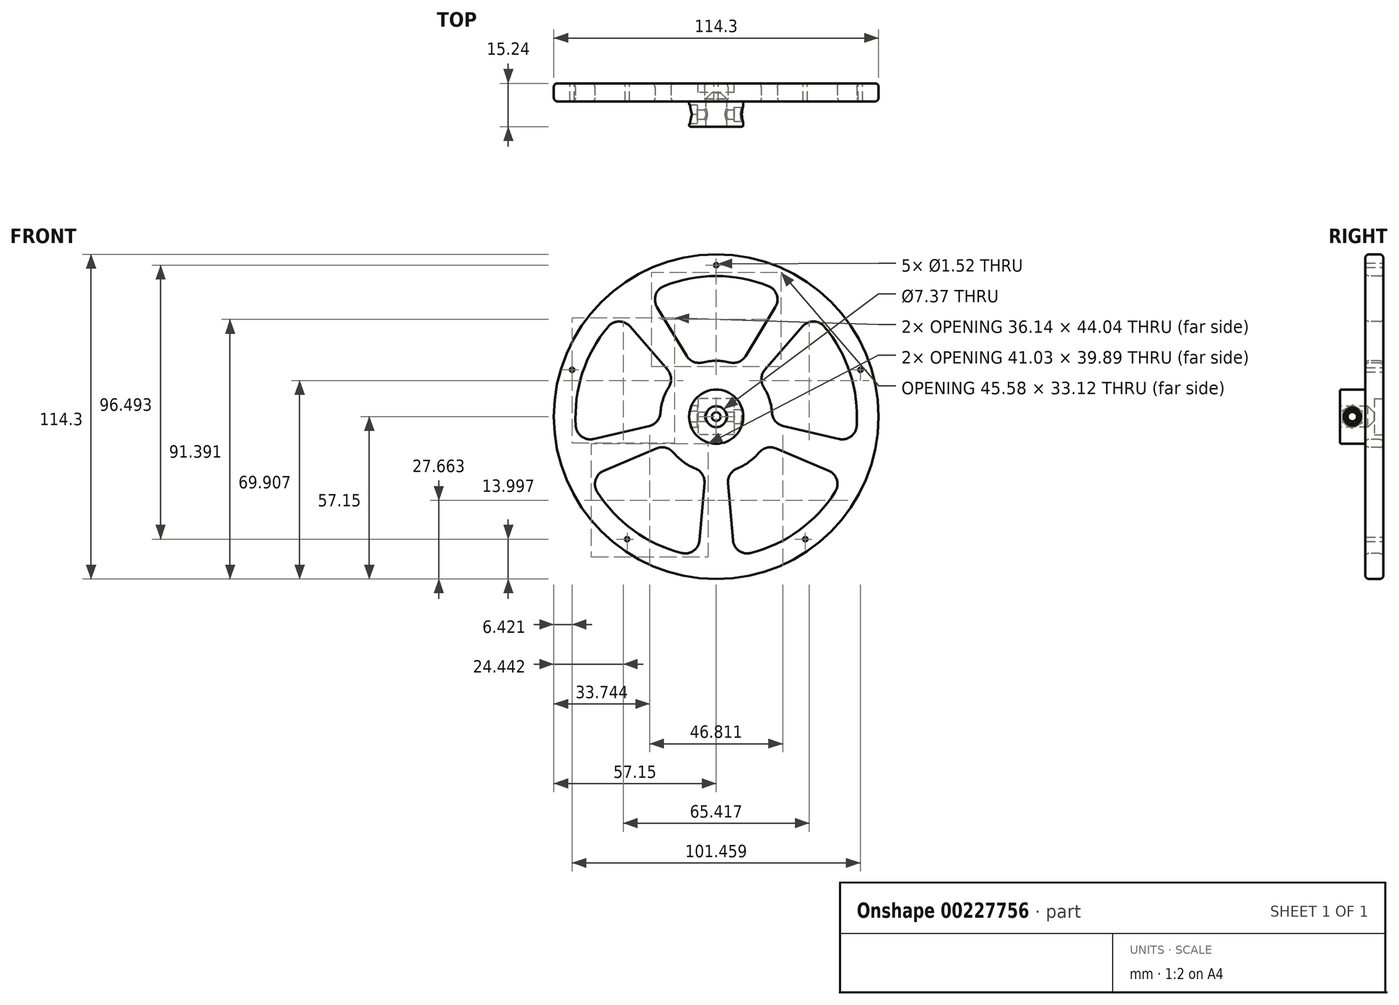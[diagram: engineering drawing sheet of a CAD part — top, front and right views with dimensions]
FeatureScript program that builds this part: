
annotation { "Feature Type Name" : "Feature", "Feature Type Description" : "" }
export const myFeature = defineFeature(function(context is Context, id is Id, definition is map)
    precondition{}
    {
        {
            var Q0;
            Q0=qCreatedBy(makeId("Front.planeOp"),FACE);
            var sketch = newSketch(context, id + "F0", { "sketchPlane" : qUnion([Q0])});
            skCircle(sketch, "E0", {"center": v(0, 0) * mm, "radius": 57.15 * mm});
            skSolve(sketch);
        }
        {
            var Q0;
            Q0 = qSketchRegion(id + "F0", true);
            extrude(context, id + "F1", {"entities" : qUnion([Q0]), "depth" : 6.35 * mm});
        }
        {
            var Q0;
            Q0=makeQuery(id+"F1.opExtrude","CAP_FACE",FACE,{"disambiguationData":[OSD([sQuery(id+"F0.wireOp",EDGE,"E0")])],"isStart":false});
            var sketch = newSketch(context, id + "F2", { "sketchPlane" : qUnion([Q0])});
            skCircle(sketch, "E1", {"center": v(0, 0) * mm, "radius": 9.53 * mm});
            skSolve(sketch);
        }
        {
            var Q0;
            Q0 = qSketchRegion(id + "F2", true);
            extrude(context, id + "F3", {"entities" : qUnion([Q0]), "operationType" : NewBodyOperationType.ADD, "depth" : 8.9 * mm});
        }
        {
            var Q0;
            Q0=makeQuery(id+"F3.opExtrude","CAP_FACE",FACE,{"disambiguationData":[OSD([sQuery(id+"F2.wireOp",EDGE,"E1")])],"isStart":false});
            var sketch = newSketch(context, id + "F4", { "sketchPlane" : qUnion([Q0])});
            skCircle(sketch, "E2", {"center": v(0, 0) * mm, "radius": 3.68 * mm});
            skSolve(sketch);
        }
        {
            var Q0;
            Q0 = qSketchRegion(id + "F4", true);
            extrude(context, id + "F5", {"entities" : qUnion([Q0]), "operationType" : NewBodyOperationType.REMOVE, "oppositeDirection" : true, "depth" : 8.9 * mm});
        }
        {
            var Q0;
            Q0=qCreatedBy(makeId("Right.planeOp"),FACE);
            var sketch = newSketch(context, id + "F6", { "sketchPlane" : qUnion([Q0])});
            skCircle(sketch, "E3", {"center": v(-10.92, 0) * mm, "radius": 1.65 * mm});
            skSolve(sketch);
        }
        {
            var Q0;
            Q0 = qSketchRegion(id + "F6", true);
            extrude(context, id + "F7", {"entities" : qUnion([Q0]), "operationType" : NewBodyOperationType.REMOVE, "oppositeDirection" : true, "depth" : 25.4 * mm, "symmetric" : true});
        }
        {
            var Q0;
            Q0=makeQuery(id+"F1.opExtrude","CAP_FACE",FACE,{"disambiguationData":[OSD([sQuery(id+"F0.wireOp",EDGE,"E0")])],"isStart":true});
            var sketch = newSketch(context, id + "F8", { "sketchPlane" : qUnion([Q0])});
            skCircle(sketch, "E4", {"center": v(0, 53.34) * mm, "radius": 0.76 * mm});
            skCircle(sketch, "E5.1.0", {"center": v(-50.73, 16.48) * mm, "radius": 0.76 * mm});
            skCircle(sketch, "E5.2.0", {"center": v(-31.35, -43.15) * mm, "radius": 0.76 * mm});
            skCircle(sketch, "E5.3.0", {"center": v(31.35, -43.15) * mm, "radius": 0.76 * mm});
            skCircle(sketch, "E5.4.0", {"center": v(50.73, 16.48) * mm, "radius": 0.76 * mm});
            skPoint(sketch, "E5.center", {"position": v(0, 0) * mm});
            skSolve(sketch);
        }
        {
            var Q0;
            Q0 = qSketchRegion(id + "F8", true);
            extrude(context, id + "F9", {"entities" : qUnion([Q0]), "operationType" : NewBodyOperationType.REMOVE, "endBound" : BoundingType.THROUGH_ALL, "oppositeDirection" : true, "depth" : 25.4 * mm});
        }
        {
            var Q0;
            Q0=makeQuery(id+"F1.opExtrude","CAP_FACE",FACE,{"disambiguationData":[OSD([sQuery(id+"F0.wireOp",EDGE,"E0")])],"isStart":false});
            var sketch = newSketch(context, id + "F10", { "sketchPlane" : qUnion([Q0])});
            skArc(sketch, "E6", {"start": v(-14.43, 13.38) * mm, "mid": v(-18.72, 6.08) * mm, "end": v(-19.54, -2.34) * mm});
            skArc(sketch, "E7", {"start": v(-34.01, 36) * mm, "mid": v(-47.1, 15.3) * mm, "end": v(-48.68, -9.14) * mm});
            skLineSegment(sketch, "E8", {"start": v(-3.8, -19.31) * mm, "end": v(-6.35, -49.12) * mm});
            skLineSegment(sketch, "E9", {"start": v(3.8, -19.31) * mm, "end": v(6.35, -49.12) * mm});
            skLineSegment(sketch, "E10.1.0", {"start": v(17.2, -9.6) * mm, "end": v(44.75, -21.22) * mm});
            skLineSegment(sketch, "E10.1.1", {"start": v(19.54, -2.34) * mm, "end": v(48.68, -9.14) * mm});
            skLineSegment(sketch, "E10.2.0", {"start": v(14.43, 13.38) * mm, "end": v(34.01, 36) * mm});
            skLineSegment(sketch, "E10.2.1", {"start": v(8.27, 17.86) * mm, "end": v(23.74, 43.47) * mm});
            skLineSegment(sketch, "E10.3.0", {"start": v(-8.27, 17.86) * mm, "end": v(-23.74, 43.47) * mm});
            skLineSegment(sketch, "E10.3.1", {"start": v(-14.43, 13.38) * mm, "end": v(-34.01, 36) * mm});
            skLineSegment(sketch, "E10.4.0", {"start": v(-19.54, -2.34) * mm, "end": v(-48.68, -9.14) * mm});
            skLineSegment(sketch, "E10.4.1", {"start": v(-17.2, -9.6) * mm, "end": v(-44.75, -21.22) * mm});
            skArc(sketch, "E11.trimOffspring", {"start": v(8.27, 17.86) * mm, "mid": v(0, 19.69) * mm, "end": v(-8.27, 17.86) * mm});
            skArc(sketch, "E12.trimOffspring", {"start": v(23.74, 43.47) * mm, "mid": v(0, 49.53) * mm, "end": v(-23.74, 43.47) * mm});
            skArc(sketch, "E13.trimOffspring", {"start": v(48.68, -9.14) * mm, "mid": v(47.1, 15.3) * mm, "end": v(34.01, 36) * mm});
            skArc(sketch, "E14.trimOffspring", {"start": v(19.54, -2.34) * mm, "mid": v(18.72, 6.08) * mm, "end": v(14.43, 13.38) * mm});
            skArc(sketch, "E15.trimOffspring", {"start": v(3.81, -19.31) * mm, "mid": v(11.57, -15.93) * mm, "end": v(17.2, -9.6) * mm});
            skArc(sketch, "E16.trimOffspring", {"start": v(6.35, -49.12) * mm, "mid": v(29.11, -40.07) * mm, "end": v(44.75, -21.22) * mm});
            skArc(sketch, "E17.trimOffspring", {"start": v(-44.75, -21.22) * mm, "mid": v(-29.11, -40.07) * mm, "end": v(-6.35, -49.12) * mm});
            skArc(sketch, "E18.trimOffspring", {"start": v(-17.2, -9.6) * mm, "mid": v(-11.57, -15.93) * mm, "end": v(-3.81, -19.31) * mm});
            skSolve(sketch);
        }
        {
            var Q0;
            Q0 = qSketchRegion(id + "F10", true);
            extrude(context, id + "F11", {"entities" : qUnion([Q0]), "operationType" : NewBodyOperationType.REMOVE, "oppositeDirection" : true, "depth" : 25.4 * mm});
        }
        {
            var Q0;
            Q0=makeQuery(id+"F11.boolean.opBoolean","COPY",EDGE,{"derivedFrom":makeQuery(id+"F11.opExtrude","SWEPT_EDGE",EDGE,{"disambiguationData":[OSD([sQuery(id+"F10.wireOp",EDGE,"E10.3.0"),sQuery(id+"F10.wireOp",EDGE,"E11.trimOffspring")])]})});
            var Q1;
            Q1=makeQuery(id+"F11.boolean.opBoolean","COPY",EDGE,{"derivedFrom":makeQuery(id+"F11.opExtrude","SWEPT_EDGE",EDGE,{"disambiguationData":[OSD([sQuery(id+"F10.wireOp",EDGE,"E10.2.1"),sQuery(id+"F10.wireOp",EDGE,"E11.trimOffspring")])]})});
            var Q2;
            Q2=makeQuery(id+"F11.boolean.opBoolean","COPY",EDGE,{"derivedFrom":makeQuery(id+"F11.opExtrude","SWEPT_EDGE",EDGE,{"disambiguationData":[OSD([sQuery(id+"F10.wireOp",EDGE,"E10.3.0"),sQuery(id+"F10.wireOp",EDGE,"E12.trimOffspring")])]})});
            var Q3;
            Q3=makeQuery(id+"F11.boolean.opBoolean","COPY",EDGE,{"derivedFrom":makeQuery(id+"F11.opExtrude","SWEPT_EDGE",EDGE,{"disambiguationData":[OSD([sQuery(id+"F10.wireOp",EDGE,"E10.2.1"),sQuery(id+"F10.wireOp",EDGE,"E12.trimOffspring")])]})});
            var Q4;
            Q4=makeQuery(id+"F11.boolean.opBoolean","COPY",EDGE,{"derivedFrom":makeQuery(id+"F11.opExtrude","SWEPT_EDGE",EDGE,{"disambiguationData":[OSD([sQuery(id+"F10.wireOp",EDGE,"E10.2.0"),sQuery(id+"F10.wireOp",EDGE,"E13.trimOffspring")])]})});
            var Q5;
            Q5=makeQuery(id+"F11.boolean.opBoolean","COPY",EDGE,{"derivedFrom":makeQuery(id+"F11.opExtrude","SWEPT_EDGE",EDGE,{"disambiguationData":[OSD([sQuery(id+"F10.wireOp",EDGE,"E10.2.0"),sQuery(id+"F10.wireOp",EDGE,"E14.trimOffspring")])]})});
            var Q6;
            Q6=makeQuery(id+"F11.boolean.opBoolean","COPY",EDGE,{"derivedFrom":makeQuery(id+"F11.opExtrude","SWEPT_EDGE",EDGE,{"disambiguationData":[OSD([sQuery(id+"F10.wireOp",EDGE,"E10.1.1"),sQuery(id+"F10.wireOp",EDGE,"E14.trimOffspring")])]})});
            var Q7;
            Q7=makeQuery(id+"F11.boolean.opBoolean","COPY",EDGE,{"derivedFrom":makeQuery(id+"F11.opExtrude","SWEPT_EDGE",EDGE,{"disambiguationData":[OSD([sQuery(id+"F10.wireOp",EDGE,"E10.1.1"),sQuery(id+"F10.wireOp",EDGE,"E13.trimOffspring")])]})});
            var Q8;
            Q8=makeQuery(id+"F11.boolean.opBoolean","COPY",EDGE,{"derivedFrom":makeQuery(id+"F11.opExtrude","SWEPT_EDGE",EDGE,{"disambiguationData":[OSD([sQuery(id+"F10.wireOp",EDGE,"E10.1.0"),sQuery(id+"F10.wireOp",EDGE,"E16.trimOffspring")])]})});
            var Q9;
            Q9=makeQuery(id+"F11.boolean.opBoolean","COPY",EDGE,{"derivedFrom":makeQuery(id+"F11.opExtrude","SWEPT_EDGE",EDGE,{"disambiguationData":[OSD([sQuery(id+"F10.wireOp",EDGE,"E9"),sQuery(id+"F10.wireOp",EDGE,"E16.trimOffspring")])]})});
            var Q10;
            Q10=makeQuery(id+"F11.boolean.opBoolean","COPY",EDGE,{"derivedFrom":makeQuery(id+"F11.opExtrude","SWEPT_EDGE",EDGE,{"disambiguationData":[OSD([sQuery(id+"F10.wireOp",EDGE,"E9"),sQuery(id+"F10.wireOp",EDGE,"E15.trimOffspring")])]})});
            var Q11;
            Q11=makeQuery(id+"F11.boolean.opBoolean","COPY",EDGE,{"derivedFrom":makeQuery(id+"F11.opExtrude","SWEPT_EDGE",EDGE,{"disambiguationData":[OSD([sQuery(id+"F10.wireOp",EDGE,"E10.1.0"),sQuery(id+"F10.wireOp",EDGE,"E15.trimOffspring")])]})});
            var Q12;
            Q12=makeQuery(id+"F11.boolean.opBoolean","COPY",EDGE,{"derivedFrom":makeQuery(id+"F11.opExtrude","SWEPT_EDGE",EDGE,{"disambiguationData":[OSD([sQuery(id+"F10.wireOp",EDGE,"E10.4.1"),sQuery(id+"F10.wireOp",EDGE,"E18.trimOffspring")])]})});
            var Q13;
            Q13=makeQuery(id+"F11.boolean.opBoolean","COPY",EDGE,{"derivedFrom":makeQuery(id+"F11.opExtrude","SWEPT_EDGE",EDGE,{"disambiguationData":[OSD([sQuery(id+"F10.wireOp",EDGE,"E8"),sQuery(id+"F10.wireOp",EDGE,"E18.trimOffspring")])]})});
            var Q14;
            Q14=makeQuery(id+"F11.boolean.opBoolean","COPY",EDGE,{"derivedFrom":makeQuery(id+"F11.opExtrude","SWEPT_EDGE",EDGE,{"disambiguationData":[OSD([sQuery(id+"F10.wireOp",EDGE,"E8"),sQuery(id+"F10.wireOp",EDGE,"E17.trimOffspring")])]})});
            var Q15;
            Q15=makeQuery(id+"F11.boolean.opBoolean","COPY",EDGE,{"derivedFrom":makeQuery(id+"F11.opExtrude","SWEPT_EDGE",EDGE,{"disambiguationData":[OSD([sQuery(id+"F10.wireOp",EDGE,"E10.4.1"),sQuery(id+"F10.wireOp",EDGE,"E17.trimOffspring")])]})});
            var Q16;
            Q16=makeQuery(id+"F11.boolean.opBoolean","COPY",EDGE,{"derivedFrom":makeQuery(id+"F11.opExtrude","SWEPT_EDGE",EDGE,{"disambiguationData":[OSD([sQuery(id+"F10.wireOp",EDGE,"E7"),sQuery(id+"F10.wireOp",EDGE,"E10.4.0")])]})});
            var Q17;
            Q17=makeQuery(id+"F11.boolean.opBoolean","COPY",EDGE,{"derivedFrom":makeQuery(id+"F11.opExtrude","SWEPT_EDGE",EDGE,{"disambiguationData":[OSD([sQuery(id+"F10.wireOp",EDGE,"E6"),sQuery(id+"F10.wireOp",EDGE,"E10.4.0")])]})});
            var Q18;
            Q18=makeQuery(id+"F11.boolean.opBoolean","COPY",EDGE,{"derivedFrom":makeQuery(id+"F11.opExtrude","SWEPT_EDGE",EDGE,{"disambiguationData":[OSD([sQuery(id+"F10.wireOp",EDGE,"E6"),sQuery(id+"F10.wireOp",EDGE,"E10.3.1")])]})});
            var Q19;
            Q19=makeQuery(id+"F11.boolean.opBoolean","COPY",EDGE,{"derivedFrom":makeQuery(id+"F11.opExtrude","SWEPT_EDGE",EDGE,{"disambiguationData":[OSD([sQuery(id+"F10.wireOp",EDGE,"E7"),sQuery(id+"F10.wireOp",EDGE,"E10.3.1")])]})});
            fillet(context, id + "F12", {"entities" : qUnion([Q0, Q1, Q2, Q3, Q4, Q5, Q6, Q7, Q8, Q9, Q10, Q11, Q12, Q13, Q14, Q15, Q16, Q17, Q18, Q19]), "radius" : 5.08 * mm, "tangentPropagation" : true, "allowEdgeOverflow" : false});
        }
        {
            var Q0;
            Q0=makeQuery(id+"F1.opExtrude","CAP_EDGE",EDGE,{"disambiguationData":[OSD([sQuery(id+"F0.wireOp",EDGE,"E0")])],"isStart":false});
            var Q1;
            Q1=makeQuery(id+"F12.opFillet","BLEND_EDGE",EDGE,{"blendedFrom":[makeQuery(id+"F11.boolean.opBoolean","COPY",EDGE,{"derivedFrom":makeQuery(id+"F11.opExtrude","SWEPT_EDGE",EDGE,{"disambiguationData":[OSD([sQuery(id+"F10.wireOp",EDGE,"E10.2.0"),sQuery(id+"F10.wireOp",EDGE,"E13.trimOffspring")])]})}),makeQuery(id+"F1.opExtrude","CAP_FACE",FACE,{"disambiguationData":[OSD([sQuery(id+"F0.wireOp",EDGE,"E0")])],"isStart":false})],"blendedInto":[makeQuery(id+"F1.opExtrude","CAP_FACE",FACE,{"disambiguationData":[OSD([sQuery(id+"F0.wireOp",EDGE,"E0")])],"isStart":false})]});
            var Q2;
            Q2=makeQuery(id+"F12.opFillet","BLEND_EDGE",EDGE,{"blendedFrom":[makeQuery(id+"F11.boolean.opBoolean","COPY",EDGE,{"derivedFrom":makeQuery(id+"F11.opExtrude","SWEPT_EDGE",EDGE,{"disambiguationData":[OSD([sQuery(id+"F10.wireOp",EDGE,"E10.2.1"),sQuery(id+"F10.wireOp",EDGE,"E11.trimOffspring")])]})}),makeQuery(id+"F1.opExtrude","CAP_FACE",FACE,{"disambiguationData":[OSD([sQuery(id+"F0.wireOp",EDGE,"E0")])],"isStart":false})],"blendedInto":[makeQuery(id+"F1.opExtrude","CAP_FACE",FACE,{"disambiguationData":[OSD([sQuery(id+"F0.wireOp",EDGE,"E0")])],"isStart":false})]});
            var Q3;
            Q3=makeQuery(id+"F12.opFillet","BLEND_EDGE",EDGE,{"blendedFrom":[makeQuery(id+"F11.boolean.opBoolean","COPY",EDGE,{"derivedFrom":makeQuery(id+"F11.opExtrude","SWEPT_EDGE",EDGE,{"disambiguationData":[OSD([sQuery(id+"F10.wireOp",EDGE,"E10.1.0"),sQuery(id+"F10.wireOp",EDGE,"E15.trimOffspring")])]})}),makeQuery(id+"F1.opExtrude","CAP_FACE",FACE,{"disambiguationData":[OSD([sQuery(id+"F0.wireOp",EDGE,"E0")])],"isStart":false})],"blendedInto":[makeQuery(id+"F1.opExtrude","CAP_FACE",FACE,{"disambiguationData":[OSD([sQuery(id+"F0.wireOp",EDGE,"E0")])],"isStart":false})]});
            var Q4;
            Q4=makeQuery(id+"F12.opFillet","BLEND_EDGE",EDGE,{"blendedFrom":[makeQuery(id+"F11.boolean.opBoolean","COPY",EDGE,{"derivedFrom":makeQuery(id+"F11.opExtrude","SWEPT_EDGE",EDGE,{"disambiguationData":[OSD([sQuery(id+"F10.wireOp",EDGE,"E10.4.1"),sQuery(id+"F10.wireOp",EDGE,"E18.trimOffspring")])]})}),makeQuery(id+"F1.opExtrude","CAP_FACE",FACE,{"disambiguationData":[OSD([sQuery(id+"F0.wireOp",EDGE,"E0")])],"isStart":false})],"blendedInto":[makeQuery(id+"F1.opExtrude","CAP_FACE",FACE,{"disambiguationData":[OSD([sQuery(id+"F0.wireOp",EDGE,"E0")])],"isStart":false})]});
            var Q5;
            Q5=makeQuery(id+"F12.opFillet","BLEND_EDGE",EDGE,{"blendedFrom":[makeQuery(id+"F11.boolean.opBoolean","COPY",EDGE,{"derivedFrom":makeQuery(id+"F11.opExtrude","SWEPT_EDGE",EDGE,{"disambiguationData":[OSD([sQuery(id+"F10.wireOp",EDGE,"E6"),sQuery(id+"F10.wireOp",EDGE,"E10.3.1")])]})}),makeQuery(id+"F1.opExtrude","CAP_FACE",FACE,{"disambiguationData":[OSD([sQuery(id+"F0.wireOp",EDGE,"E0")])],"isStart":false})],"blendedInto":[makeQuery(id+"F1.opExtrude","CAP_FACE",FACE,{"disambiguationData":[OSD([sQuery(id+"F0.wireOp",EDGE,"E0")])],"isStart":false})]});
            var Q6;
            Q6=makeQuery(id+"F11.boolean.opBoolean","INTERSECT",EDGE,{"derivedFrom":[makeQuery(id+"F1.opExtrude","CAP_FACE",FACE,{"disambiguationData":[OSD([sQuery(id+"F0.wireOp",EDGE,"E0")])],"isStart":true}),makeQuery(id+"F11.opExtrude","SWEPT_FACE",FACE,{"disambiguationData":[OSD([sQuery(id+"F10.wireOp",EDGE,"E12.trimOffspring")])]})]});
            var Q7;
            Q7=makeQuery(id+"F11.boolean.opBoolean","INTERSECT",EDGE,{"derivedFrom":[makeQuery(id+"F1.opExtrude","CAP_FACE",FACE,{"disambiguationData":[OSD([sQuery(id+"F0.wireOp",EDGE,"E0")])],"isStart":true}),makeQuery(id+"F11.opExtrude","SWEPT_FACE",FACE,{"disambiguationData":[OSD([sQuery(id+"F10.wireOp",EDGE,"E10.2.0")])]})]});
            var Q8;
            Q8=makeQuery(id+"F11.boolean.opBoolean","INTERSECT",EDGE,{"derivedFrom":[makeQuery(id+"F1.opExtrude","CAP_FACE",FACE,{"disambiguationData":[OSD([sQuery(id+"F0.wireOp",EDGE,"E0")])],"isStart":true}),makeQuery(id+"F11.opExtrude","SWEPT_FACE",FACE,{"disambiguationData":[OSD([sQuery(id+"F10.wireOp",EDGE,"E10.1.0")])]})]});
            var Q9;
            Q9=makeQuery(id+"F12.opFillet","BLEND_EDGE",EDGE,{"blendedFrom":[makeQuery(id+"F11.boolean.opBoolean","COPY",EDGE,{"derivedFrom":makeQuery(id+"F11.opExtrude","SWEPT_EDGE",EDGE,{"disambiguationData":[OSD([sQuery(id+"F10.wireOp",EDGE,"E8"),sQuery(id+"F10.wireOp",EDGE,"E18.trimOffspring")])]})}),makeQuery(id+"F1.opExtrude","CAP_FACE",FACE,{"disambiguationData":[OSD([sQuery(id+"F0.wireOp",EDGE,"E0")])],"isStart":true})],"blendedInto":[makeQuery(id+"F1.opExtrude","CAP_FACE",FACE,{"disambiguationData":[OSD([sQuery(id+"F0.wireOp",EDGE,"E0")])],"isStart":true})]});
            var Q10;
            Q10=makeQuery(id+"F11.boolean.opBoolean","INTERSECT",EDGE,{"derivedFrom":[makeQuery(id+"F1.opExtrude","CAP_FACE",FACE,{"disambiguationData":[OSD([sQuery(id+"F0.wireOp",EDGE,"E0")])],"isStart":true}),makeQuery(id+"F11.opExtrude","SWEPT_FACE",FACE,{"disambiguationData":[OSD([sQuery(id+"F10.wireOp",EDGE,"E10.3.1")])]})]});
            var Q11;
            Q11=makeQuery(id+"F1.opExtrude","CAP_EDGE",EDGE,{"disambiguationData":[OSD([sQuery(id+"F0.wireOp",EDGE,"E0")])],"isStart":true});
            fillet(context, id + "F13", {"entities" : qUnion([Q0, Q1, Q2, Q3, Q4, Q5, Q6, Q7, Q8, Q9, Q10, Q11]), "radius" : 1.27 * mm, "tangentPropagation" : true, "allowEdgeOverflow" : false});
        }
        {
            var Q0;
            Q0=makeQuery(id+"F9.boolean.opBoolean","COPY",EDGE,{"derivedFrom":makeQuery(id+"F9.opExtrude","CAP_EDGE",EDGE,{"disambiguationData":[OSD([sQuery(id+"F8.wireOp",EDGE,"E5.1.0")])],"isStart":true})});
            var Q1;
            Q1=makeQuery(id+"F9.boolean.opBoolean","COPY",EDGE,{"derivedFrom":makeQuery(id+"F9.opExtrude","CAP_EDGE",EDGE,{"disambiguationData":[OSD([sQuery(id+"F8.wireOp",EDGE,"E4")])],"isStart":true})});
            var Q2;
            Q2=makeQuery(id+"F9.boolean.opBoolean","COPY",EDGE,{"derivedFrom":makeQuery(id+"F9.opExtrude","CAP_EDGE",EDGE,{"disambiguationData":[OSD([sQuery(id+"F8.wireOp",EDGE,"E5.4.0")])],"isStart":true})});
            var Q3;
            Q3=makeQuery(id+"F9.boolean.opBoolean","COPY",EDGE,{"derivedFrom":makeQuery(id+"F9.opExtrude","CAP_EDGE",EDGE,{"disambiguationData":[OSD([sQuery(id+"F8.wireOp",EDGE,"E5.3.0")])],"isStart":true})});
            var Q4;
            Q4=makeQuery(id+"F9.boolean.opBoolean","COPY",EDGE,{"derivedFrom":makeQuery(id+"F9.opExtrude","CAP_EDGE",EDGE,{"disambiguationData":[OSD([sQuery(id+"F8.wireOp",EDGE,"E5.2.0")])],"isStart":true})});
            var Q5;
            Q5=makeQuery(id+"F9.boolean.opBoolean","INTERSECT",EDGE,{"derivedFrom":[makeQuery(id+"F1.opExtrude","CAP_FACE",FACE,{"disambiguationData":[OSD([sQuery(id+"F0.wireOp",EDGE,"E0")])],"isStart":false}),makeQuery(id+"F9.opExtrude","SWEPT_FACE",FACE,{"disambiguationData":[OSD([sQuery(id+"F8.wireOp",EDGE,"E5.3.0")])]})]});
            var Q6;
            Q6=makeQuery(id+"F9.boolean.opBoolean","INTERSECT",EDGE,{"derivedFrom":[makeQuery(id+"F1.opExtrude","CAP_FACE",FACE,{"disambiguationData":[OSD([sQuery(id+"F0.wireOp",EDGE,"E0")])],"isStart":false}),makeQuery(id+"F9.opExtrude","SWEPT_FACE",FACE,{"disambiguationData":[OSD([sQuery(id+"F8.wireOp",EDGE,"E5.2.0")])]})]});
            var Q7;
            Q7=makeQuery(id+"F9.boolean.opBoolean","INTERSECT",EDGE,{"derivedFrom":[makeQuery(id+"F1.opExtrude","CAP_FACE",FACE,{"disambiguationData":[OSD([sQuery(id+"F0.wireOp",EDGE,"E0")])],"isStart":false}),makeQuery(id+"F9.opExtrude","SWEPT_FACE",FACE,{"disambiguationData":[OSD([sQuery(id+"F8.wireOp",EDGE,"E5.1.0")])]})]});
            var Q8;
            Q8=makeQuery(id+"F9.boolean.opBoolean","INTERSECT",EDGE,{"derivedFrom":[makeQuery(id+"F1.opExtrude","CAP_FACE",FACE,{"disambiguationData":[OSD([sQuery(id+"F0.wireOp",EDGE,"E0")])],"isStart":false}),makeQuery(id+"F9.opExtrude","SWEPT_FACE",FACE,{"disambiguationData":[OSD([sQuery(id+"F8.wireOp",EDGE,"E4")])]})]});
            var Q9;
            Q9=makeQuery(id+"F9.boolean.opBoolean","INTERSECT",EDGE,{"derivedFrom":[makeQuery(id+"F1.opExtrude","CAP_FACE",FACE,{"disambiguationData":[OSD([sQuery(id+"F0.wireOp",EDGE,"E0")])],"isStart":false}),makeQuery(id+"F9.opExtrude","SWEPT_FACE",FACE,{"disambiguationData":[OSD([sQuery(id+"F8.wireOp",EDGE,"E5.4.0")])]})]});
            var Q10;
            Q10=makeQuery(id+"F3.opExtrude","CAP_EDGE",EDGE,{"disambiguationData":[OSD([sQuery(id+"F2.wireOp",EDGE,"E1")])],"isStart":true});
            var Q11;
            Q11=makeQuery(id+"F3.opExtrude","CAP_EDGE",EDGE,{"disambiguationData":[OSD([sQuery(id+"F2.wireOp",EDGE,"E1")])],"isStart":false});
            var Q12;
            Q12=makeQuery(id+"F5.boolean.opBoolean","COPY",EDGE,{"derivedFrom":makeQuery(id+"F5.opExtrude","CAP_EDGE",EDGE,{"disambiguationData":[OSD([sQuery(id+"F4.wireOp",EDGE,"E2")])],"isStart":true})});
            var Q13;
            Q13=makeQuery(id+"F7.boolean.opBoolean","INTERSECT",EDGE,{"disambiguationData":[OD(0.0)],"derivedFrom":[makeQuery(id+"F5.boolean.opBoolean","COPY",FACE,{"derivedFrom":makeQuery(id+"F5.opExtrude","SWEPT_FACE",FACE,{"disambiguationData":[OSD([sQuery(id+"F4.wireOp",EDGE,"E2")])]})}),makeQuery(id+"F7.opExtrude","SWEPT_FACE",FACE,{"disambiguationData":[OSD([sQuery(id+"F6.wireOp",EDGE,"E3")])]})]});
            var Q14;
            Q14=makeQuery(id+"F7.boolean.opBoolean","INTERSECT",EDGE,{"disambiguationData":[OD(1.0)],"derivedFrom":[makeQuery(id+"F5.boolean.opBoolean","COPY",FACE,{"derivedFrom":makeQuery(id+"F5.opExtrude","SWEPT_FACE",FACE,{"disambiguationData":[OSD([sQuery(id+"F4.wireOp",EDGE,"E2")])]})}),makeQuery(id+"F7.opExtrude","SWEPT_FACE",FACE,{"disambiguationData":[OSD([sQuery(id+"F6.wireOp",EDGE,"E3")])]})]});
            var Q15;
            Q15=makeQuery(id+"F7.boolean.opBoolean","INTERSECT",EDGE,{"disambiguationData":[OD(1.0)],"derivedFrom":[makeQuery(id+"F3.opExtrude","SWEPT_FACE",FACE,{"disambiguationData":[OSD([sQuery(id+"F2.wireOp",EDGE,"E1")])]}),makeQuery(id+"F7.opExtrude","SWEPT_FACE",FACE,{"disambiguationData":[OSD([sQuery(id+"F6.wireOp",EDGE,"E3")])]})]});
            fillet(context, id + "F14", {"entities" : qUnion([Q0, Q1, Q2, Q3, Q4, Q5, Q6, Q7, Q8, Q9, Q10, Q11, Q12, Q13, Q14, Q15]), "radius" : 0.5 * mm, "tangentPropagation" : true, "allowEdgeOverflow" : false});
        }
        {
            var Q0;
            Q0=makeQuery(id+"F1.opExtrude","CAP_FACE",FACE,{"disambiguationData":[OSD([sQuery(id+"F0.wireOp",EDGE,"E0")])],"isStart":true});
            var sketch = newSketch(context, id + "F15", { "sketchPlane" : qUnion([Q0])});
            skLineSegment(sketch, "E19.bottom", {"start": v(-6.35, 6.35) * mm, "end": v(6.35, 6.35) * mm});
            skLineSegment(sketch, "E19.top", {"start": v(-6.35, -6.35) * mm, "end": v(6.35, -6.35) * mm});
            skLineSegment(sketch, "E19.left", {"start": v(-6.35, 6.35) * mm, "end": v(-6.35, -6.35) * mm});
            skLineSegment(sketch, "E19.right", {"start": v(6.35, 6.35) * mm, "end": v(6.35, -6.35) * mm});
            skSolve(sketch);
        }
        {
            var Q0;
            Q0 = qSketchRegion(id + "F15", true);
            extrude(context, id + "F16", {"entities" : qUnion([Q0]), "operationType" : NewBodyOperationType.REMOVE, "oppositeDirection" : true, "depth" : 3.17 * mm});
        }
        {
            var Q0;
            Q0=makeQuery(id+"F16.boolean.opBoolean","COPY",FACE,{"derivedFrom":makeQuery(id+"F16.opExtrude","CAP_FACE",FACE,{"disambiguationData":[OSD([sQuery(id+"F15.wireOp",EDGE,"E19.bottom"),sQuery(id+"F15.wireOp",EDGE,"E19.top"),sQuery(id+"F15.wireOp",EDGE,"E19.left"),sQuery(id+"F15.wireOp",EDGE,"E19.right")])],"isStart":false})});
            var sketch = newSketch(context, id + "F17", { "sketchPlane" : qUnion([Q0])});
            skCircle(sketch, "E20", {"center": v(0, 0) * mm, "radius": 1.52 * mm});
            skSolve(sketch);
        }
        {
            var Q0;
            Q0 = qSketchRegion(id + "F17", true);
            extrude(context, id + "F18", {"entities" : qUnion([Q0]), "operationType" : NewBodyOperationType.REMOVE, "oppositeDirection" : true, "depth" : 25.4 * mm});
        }
        {
            var Q0;
            Q0=makeQuery(id+"F18.boolean.opBoolean","INTERSECT",EDGE,{"derivedFrom":[makeQuery(id+"F5.boolean.opBoolean","COPY",FACE,{"derivedFrom":makeQuery(id+"F5.opExtrude","CAP_FACE",FACE,{"disambiguationData":[OSD([sQuery(id+"F4.wireOp",EDGE,"E2")])],"isStart":false})}),makeQuery(id+"F18.opExtrude","SWEPT_FACE",FACE,{"disambiguationData":[OSD([sQuery(id+"F17.wireOp",EDGE,"E20")])]})]});
            chamfer(context, id + "F19", {"entities" : qUnion([Q0]), "width" : 3.05 * mm, "tangentPropagation" : true});
        }
        {
            var Q0;
            Q0=qCreatedBy(makeId("Right.planeOp"),FACE);
            cPlane(context, id + "F20", {"entities" : qUnion([Q0]), "cplaneType" : CPlaneType.OFFSET, "offset" : 12.7 * mm, "oppositeDirection" : true, "width" : 152.4 * mm, "height" : 152.4 * mm});
        }
        {
            var Q0;
            Q0=qCreatedBy(id+"F20.planeOp",FACE);
            var sketch = newSketch(context, id + "F21", { "sketchPlane" : qUnion([Q0])});
            skCircle(sketch, "E21.cCircle", {"center": v(-10.92, 0) * mm, "radius": 3.3 * mm, "construction": true});
            skLineSegment(sketch, "E21.0", {"start": v(-14.22, -1.9) * mm, "end": v(-14.22, 1.9) * mm});
            skLineSegment(sketch, "E21.1", {"start": v(-14.22, 1.9) * mm, "end": v(-10.92, 3.81) * mm});
            skLineSegment(sketch, "E21.2", {"start": v(-10.92, 3.81) * mm, "end": v(-7.62, 1.9) * mm});
            skLineSegment(sketch, "E21.3", {"start": v(-7.62, 1.9) * mm, "end": v(-7.62, -1.9) * mm});
            skLineSegment(sketch, "E21.4", {"start": v(-7.62, -1.9) * mm, "end": v(-10.92, -3.81) * mm});
            skLineSegment(sketch, "E21.5", {"start": v(-10.92, -3.81) * mm, "end": v(-14.22, -1.9) * mm});
            skPoint(sketch, "E21.0.midPoint", {"position": v(-14.22, 0) * mm});
            skSolve(sketch);
        }
        {
            var Q0;
            Q0 = qSketchRegion(id + "F21", true);
            extrude(context, id + "F22", {"entities" : qUnion([Q0]), "operationType" : NewBodyOperationType.REMOVE, "depth" : 6.1 * mm});
        }
        {
            var Q0;
            Q0=makeQuery(id+"F22.boolean.opBoolean","INTERSECT",EDGE,{"derivedFrom":[makeQuery(id+"F3.opExtrude","SWEPT_FACE",FACE,{"disambiguationData":[OSD([sQuery(id+"F2.wireOp",EDGE,"E1")])]}),makeQuery(id+"F22.opExtrude","SWEPT_FACE",FACE,{"disambiguationData":[OSD([sQuery(id+"F21.wireOp",EDGE,"E21.2")])]})]});
            var Q1;
            Q1=makeQuery(id+"F22.boolean.opBoolean","INTERSECT",EDGE,{"derivedFrom":[makeQuery(id+"F3.opExtrude","SWEPT_FACE",FACE,{"disambiguationData":[OSD([sQuery(id+"F2.wireOp",EDGE,"E1")])]}),makeQuery(id+"F22.opExtrude","SWEPT_FACE",FACE,{"disambiguationData":[OSD([sQuery(id+"F21.wireOp",EDGE,"E21.1")])]})]});
            var Q2;
            Q2=makeQuery(id+"F22.boolean.opBoolean","INTERSECT",EDGE,{"derivedFrom":[makeQuery(id+"F3.opExtrude","SWEPT_FACE",FACE,{"disambiguationData":[OSD([sQuery(id+"F2.wireOp",EDGE,"E1")])]}),makeQuery(id+"F22.opExtrude","SWEPT_FACE",FACE,{"disambiguationData":[OSD([sQuery(id+"F21.wireOp",EDGE,"E21.0")])]})]});
            var Q3;
            Q3=makeQuery(id+"F22.boolean.opBoolean","INTERSECT",EDGE,{"derivedFrom":[makeQuery(id+"F3.opExtrude","SWEPT_FACE",FACE,{"disambiguationData":[OSD([sQuery(id+"F2.wireOp",EDGE,"E1")])]}),makeQuery(id+"F22.opExtrude","SWEPT_FACE",FACE,{"disambiguationData":[OSD([sQuery(id+"F21.wireOp",EDGE,"E21.5")])]})]});
            var Q4;
            Q4=makeQuery(id+"F22.boolean.opBoolean","INTERSECT",EDGE,{"derivedFrom":[makeQuery(id+"F3.opExtrude","SWEPT_FACE",FACE,{"disambiguationData":[OSD([sQuery(id+"F2.wireOp",EDGE,"E1")])]}),makeQuery(id+"F22.opExtrude","SWEPT_FACE",FACE,{"disambiguationData":[OSD([sQuery(id+"F21.wireOp",EDGE,"E21.4")])]})]});
            var Q5;
            Q5=makeQuery(id+"F22.boolean.opBoolean","INTERSECT",EDGE,{"derivedFrom":[makeQuery(id+"F3.opExtrude","SWEPT_FACE",FACE,{"disambiguationData":[OSD([sQuery(id+"F2.wireOp",EDGE,"E1")])]}),makeQuery(id+"F22.opExtrude","SWEPT_FACE",FACE,{"disambiguationData":[OSD([sQuery(id+"F21.wireOp",EDGE,"E21.3")])]})]});
            var Q6;
            Q6=makeQuery(id+"F22.boolean.opBoolean","INTERSECT",EDGE,{"derivedFrom":[makeQuery(id+"F7.boolean.opBoolean","COPY",FACE,{"disambiguationData":[OD(0.0)],"derivedFrom":makeQuery(id+"F7.opExtrude","SWEPT_FACE",FACE,{"disambiguationData":[OSD([sQuery(id+"F6.wireOp",EDGE,"E3")])]})}),makeQuery(id+"F22.opExtrude","CAP_FACE",FACE,{"disambiguationData":[OSD([sQuery(id+"F21.wireOp",EDGE,"E21.0"),sQuery(id+"F21.wireOp",EDGE,"E21.1"),sQuery(id+"F21.wireOp",EDGE,"E21.2"),sQuery(id+"F21.wireOp",EDGE,"E21.3"),sQuery(id+"F21.wireOp",EDGE,"E21.4"),sQuery(id+"F21.wireOp",EDGE,"E21.5")])],"isStart":false})]});
            fillet(context, id + "F23", {"entities" : qUnion([Q0, Q1, Q2, Q3, Q4, Q5, Q6]), "radius" : 0.25 * mm, "tangentPropagation" : true, "allowEdgeOverflow" : false});
        }
        {
            var Q0;
            Q0=qCreatedBy(makeId("Right.planeOp"),FACE);
            cPlane(context, id + "F24", {"entities" : qUnion([Q0]), "cplaneType" : CPlaneType.OFFSET, "offset" : 12.7 * mm, "width" : 152.4 * mm, "height" : 152.4 * mm});
        }
        {
            var Q0;
            Q0=qCreatedBy(id+"F24.planeOp",FACE);
            var sketch = newSketch(context, id + "F25", { "sketchPlane" : qUnion([Q0])});
            skCircle(sketch, "E22", {"center": v(-10.92, 0) * mm, "radius": 2.48 * mm});
            skSolve(sketch);
        }
        {
            var Q0;
            Q0 = qSketchRegion(id + "F25", true);
            extrude(context, id + "F26", {"entities" : qUnion([Q0]), "operationType" : NewBodyOperationType.REMOVE, "oppositeDirection" : true, "depth" : 6.35 * mm});
        }
        {
            var Q0;
            Q0=makeQuery(id+"F26.boolean.opBoolean","INTERSECT",EDGE,{"derivedFrom":[makeQuery(id+"F3.opExtrude","SWEPT_FACE",FACE,{"disambiguationData":[OSD([sQuery(id+"F2.wireOp",EDGE,"E1")])]}),makeQuery(id+"F26.opExtrude","SWEPT_FACE",FACE,{"disambiguationData":[OSD([sQuery(id+"F25.wireOp",EDGE,"E22")])]})]});
            fillet(context, id + "F27", {"entities" : qUnion([Q0]), "radius" : 0.5 * mm, "tangentPropagation" : true, "allowEdgeOverflow" : false});
        }
        {
            var Q0;
            Q0=makeQuery(id+"F26.boolean.opBoolean","INTERSECT",EDGE,{"derivedFrom":[makeQuery(id+"F7.boolean.opBoolean","COPY",FACE,{"disambiguationData":[OD(1.0)],"derivedFrom":makeQuery(id+"F7.opExtrude","SWEPT_FACE",FACE,{"disambiguationData":[OSD([sQuery(id+"F6.wireOp",EDGE,"E3")])]})}),makeQuery(id+"F26.opExtrude","CAP_FACE",FACE,{"disambiguationData":[OSD([sQuery(id+"F25.wireOp",EDGE,"E22")])],"isStart":false})]});
            fillet(context, id + "F28", {"entities" : qUnion([Q0]), "radius" : 0.25 * mm, "tangentPropagation" : true, "allowEdgeOverflow" : false});
        }
    });
